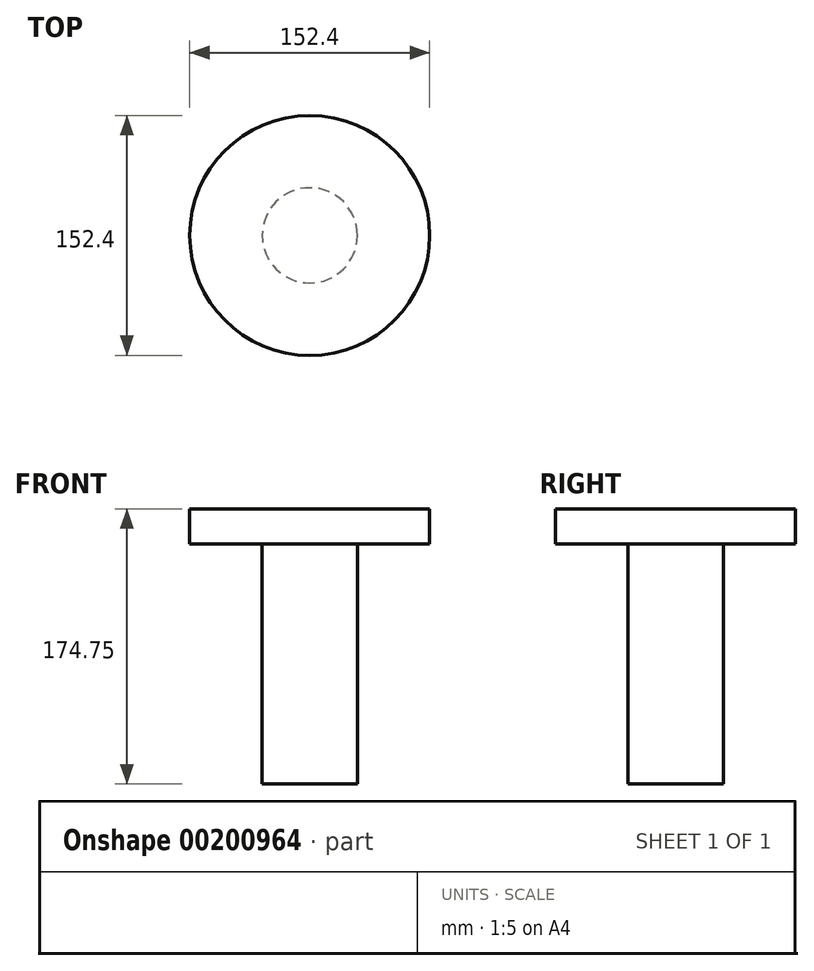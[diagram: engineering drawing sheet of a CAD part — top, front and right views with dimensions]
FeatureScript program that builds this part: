
annotation { "Feature Type Name" : "Feature", "Feature Type Description" : "" }
export const myFeature = defineFeature(function(context is Context, id is Id, definition is map)
    precondition{}
    {
        {
            var Q0;
            Q0=qCreatedBy(makeId("Front.planeOp"),FACE);
            var sketch = newSketch(context, id + "F0", { "sketchPlane" : qUnion([Q0])});
            skLineSegment(sketch, "E0", {"start": v(0, 0) * mm, "end": v(0, 335.65) * mm});
            skLineSegment(sketch, "E1", {"start": v(0, 0) * mm, "end": v(0, 174.75) * mm});
            skLineSegment(sketch, "E2", {"start": v(0, 174.75) * mm, "end": v(76.2, 174.75) * mm});
            skLineSegment(sketch, "E3", {"start": v(76.2, 174.75) * mm, "end": v(76.2, 152.4) * mm});
            skLineSegment(sketch, "E4", {"start": v(76.2, 152.4) * mm, "end": v(30.23, 152.4) * mm});
            skLineSegment(sketch, "E5", {"start": v(30.23, 152.4) * mm, "end": v(30.23, 0) * mm});
            skLineSegment(sketch, "E6", {"start": v(30.23, 0) * mm, "end": v(0, 0) * mm});
            skSolve(sketch);
        }
        {
            var Q0;
            {var subQ0=sQuery(id+"F0.wireOp",EDGE,"E2");Q0=makeQuery(id+"F0.imprint","IMPRINT",FACE,{"disambiguationData":[TD([[makeQuery(id+"F0.imprint","IMPRINT",EDGE,{"derivedFrom":subQ0}),-1.0]])]});}
            var Q1;
            Q1=sQuery(id+"F0.wireOp",EDGE,"E0");
            revolve(context, id + "F1", {"surfaceOperationType" : NewSurfaceOperationType.NEW, "entities" : qUnion([Q0]), "axis" : qUnion([Q1]), "revolveType" : RevolveType.FULL});
        }
    });
